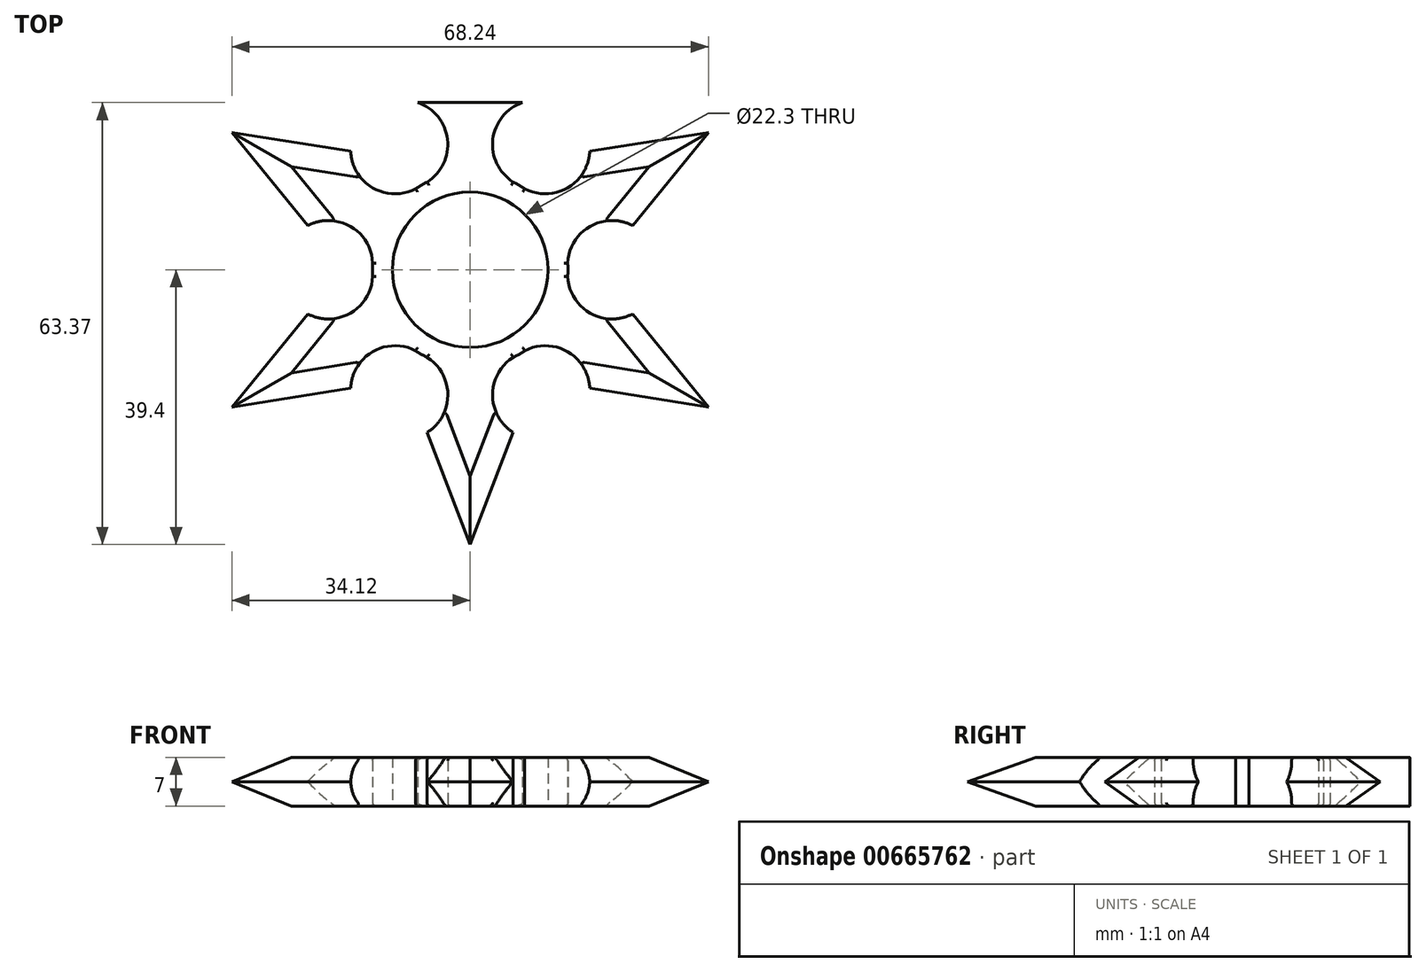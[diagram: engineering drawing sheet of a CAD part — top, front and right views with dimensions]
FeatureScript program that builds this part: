
annotation { "Feature Type Name" : "Feature", "Feature Type Description" : "" }
export const myFeature = defineFeature(function(context is Context, id is Id, definition is map)
    precondition{}
    {
        {
            var Q0;
            Q0=qCreatedBy(makeId("Top.planeOp"),FACE);
            var sketch = newSketch(context, id + "F0", { "sketchPlane" : qUnion([Q0])});
            skCircle(sketch, "E0", {"center": v(0, 0) * mm, "radius": 11.15 * mm});
            skCircle(sketch, "E1", {"center": v(0, 0) * mm, "radius": 14 * mm});
            skLineSegment(sketch, "E2", {"start": v(0, 0) * mm, "end": v(0, 43.6) * mm});
            skLineSegment(sketch, "E3", {"start": v(0, 0) * mm, "end": v(37.76, 21.8) * mm});
            skLineSegment(sketch, "E4.MirrorCS", {"start": v(0, 0) * mm, "end": v(37.76, -21.8) * mm});
            skLineSegment(sketch, "E5.MirrorCS", {"start": v(0, 0) * mm, "end": v(-37.76, -21.8) * mm});
            skLineSegment(sketch, "E6.MirrorCS", {"start": v(0, 0) * mm, "end": v(-37.76, 21.8) * mm});
            skLineSegment(sketch, "E7", {"start": v(0, 0) * mm, "end": v(0, -43.6) * mm});
            skLineSegment(sketch, "E8", {"start": v(37.76, 21.8) * mm, "end": v(24.77, 14.3) * mm});
            skLineSegment(sketch, "E9", {"start": v(37.76, 21.8) * mm, "end": v(20.76, 11.98) * mm});
            skLineSegment(sketch, "E10", {"start": v(20.76, 11.98) * mm, "end": v(24.5, 5.49) * mm});
            skLineSegment(sketch, "E11.MirrorCS", {"start": v(20.76, 11.98) * mm, "end": v(17, 18.48) * mm});
            skLineSegment(sketch, "E12", {"start": v(37.76, 21.8) * mm, "end": v(17, 18.48) * mm});
            skLineSegment(sketch, "E13", {"start": v(24.5, 5.49) * mm, "end": v(37.76, 21.8) * mm});
            skLineSegment(sketch, "E14", {"start": v(0, 0) * mm, "end": v(7, 12.12) * mm});
            skArc(sketch, "E15", {"start": v(7, 12.12) * mm, "mid": v(14.18, 11.88) * mm, "end": v(17, 18.48) * mm});
            skArc(sketch, "E16.MirrorCS", {"start": v(14, 0) * mm, "mid": v(17.38, 6.34) * mm, "end": v(24.5, 5.49) * mm});
            skLineSegment(sketch, "E17.MirrorCS", {"start": v(-37.76, 21.8) * mm, "end": v(-17, 18.48) * mm});
            skLineSegment(sketch, "E18.MirrorCS", {"start": v(-20.76, 11.98) * mm, "end": v(-17, 18.48) * mm});
            skArc(sketch, "E19.MirrorCS", {"start": v(-7, 12.12) * mm, "mid": v(-14.18, 11.88) * mm, "end": v(-17, 18.48) * mm});
            skArc(sketch, "E20.MirrorCS", {"start": v(-14, 0) * mm, "mid": v(-17.38, 6.34) * mm, "end": v(-24.5, 5.49) * mm});
            skLineSegment(sketch, "E21.MirrorCS", {"start": v(-20.76, 11.98) * mm, "end": v(-24.5, 5.49) * mm});
            skLineSegment(sketch, "E22.MirrorCS", {"start": v(-24.5, 5.49) * mm, "end": v(-37.76, 21.8) * mm});
            skArc(sketch, "E23.MirrorCS", {"start": v(7, -12.12) * mm, "mid": v(14.18, -11.88) * mm, "end": v(17, -18.48) * mm});
            skLineSegment(sketch, "E24.MirrorCS", {"start": v(37.76, -21.8) * mm, "end": v(17, -18.48) * mm});
            skLineSegment(sketch, "E25.MirrorCS", {"start": v(20.76, -11.98) * mm, "end": v(17, -18.48) * mm});
            skArc(sketch, "E26.MirrorCS", {"start": v(14, 0) * mm, "mid": v(17.38, -6.34) * mm, "end": v(24.5, -5.49) * mm});
            skLineSegment(sketch, "E27.MirrorCS", {"start": v(20.76, -11.98) * mm, "end": v(24.5, -5.49) * mm});
            skLineSegment(sketch, "E28.MirrorCS", {"start": v(24.5, -5.49) * mm, "end": v(37.76, -21.8) * mm});
            skArc(sketch, "E29.MirrorCS", {"start": v(-14, 0) * mm, "mid": v(-17.38, -6.34) * mm, "end": v(-24.5, -5.49) * mm});
            skLineSegment(sketch, "E30.MirrorCS", {"start": v(-20.76, -11.98) * mm, "end": v(-24.5, -5.49) * mm});
            skLineSegment(sketch, "E31.MirrorCS", {"start": v(-24.5, -5.49) * mm, "end": v(-37.76, -21.8) * mm});
            skLineSegment(sketch, "E32.MirrorCS", {"start": v(-37.76, -21.8) * mm, "end": v(-17, -18.48) * mm});
            skArc(sketch, "E33.MirrorCS", {"start": v(-7, -12.12) * mm, "mid": v(-14.18, -11.88) * mm, "end": v(-17, -18.48) * mm});
            skLineSegment(sketch, "E34.MirrorCS", {"start": v(-20.76, -11.98) * mm, "end": v(-17, -18.48) * mm});
            skLineSegment(sketch, "E35", {"start": v(0, 43.6) * mm, "end": v(0, 23.97) * mm});
            skLineSegment(sketch, "E36", {"start": v(0, 23.97) * mm, "end": v(7.5, 23.97) * mm});
            skLineSegment(sketch, "E37", {"start": v(0, 43.6) * mm, "end": v(7.5, 23.97) * mm});
            skLineSegment(sketch, "E38.MirrorCS", {"start": v(0, 43.6) * mm, "end": v(-7.5, 23.97) * mm});
            skLineSegment(sketch, "E39.MirrorCS", {"start": v(0, 23.97) * mm, "end": v(-7.5, 23.97) * mm});
            skLineSegment(sketch, "E40", {"start": v(0, 0) * mm, "end": v(-7, 12.12) * mm});
            skLineSegment(sketch, "E41.MirrorCS", {"start": v(0, -43.6) * mm, "end": v(-7.5, -23.97) * mm});
            skLineSegment(sketch, "E42.MirrorCS", {"start": v(0, -23.97) * mm, "end": v(-7.5, -23.97) * mm});
            skLineSegment(sketch, "E43.MirrorCS", {"start": v(0, -23.97) * mm, "end": v(7.5, -23.97) * mm});
            skLineSegment(sketch, "E44.MirrorCS", {"start": v(0, -43.6) * mm, "end": v(7.5, -23.97) * mm});
            skArc(sketch, "E45", {"start": v(7, -12.12) * mm, "mid": v(3.2, -18.22) * mm, "end": v(7.5, -23.97) * mm});
            skArc(sketch, "E46.MirrorCS", {"start": v(-7, -12.12) * mm, "mid": v(-3.2, -18.22) * mm, "end": v(-7.5, -23.97) * mm});
            skArc(sketch, "E47.MirrorCS", {"start": v(7, 12.12) * mm, "mid": v(3.2, 18.22) * mm, "end": v(7.5, 23.97) * mm});
            skArc(sketch, "E48.MirrorCS", {"start": v(-7, 12.12) * mm, "mid": v(-3.2, 18.22) * mm, "end": v(-7.5, 23.97) * mm});
            skSolve(sketch);
        }
        {
            var Q0;
            Q0=makeQuery(id+"F0.imprint","IMPRINT",FACE,{"disambiguationData":[TD([[makeQuery(id+"F0.imprint","IMPRINT",EDGE,{"derivedFrom":sQuery(id+"F0.wireOp",EDGE,"E35")}),1.0]])]});
            var Q1;
            Q1=makeQuery(id+"F0.imprint","IMPRINT",FACE,{"disambiguationData":[TD([[makeQuery(id+"F0.imprint","IMPRINT",EDGE,{"derivedFrom":sQuery(id+"F0.wireOp",EDGE,"E35")}),-1.0]])]});
            var Q2;
            {var subQ5=sQuery(id+"F0.wireOp",EDGE,"E39.MirrorCS");Q2=makeQuery(id+"F0.imprint","IMPRINT",FACE,{"disambiguationData":[TD([[makeQuery(id+"F0.imprint","IMPRINT",EDGE,{"derivedFrom":subQ5}),1.0]])]});}
            var Q3;
            {var subQ5=sQuery(id+"F0.wireOp",EDGE,"E36");Q3=makeQuery(id+"F0.imprint","IMPRINT",FACE,{"disambiguationData":[TD([[makeQuery(id+"F0.imprint","IMPRINT",EDGE,{"derivedFrom":subQ5}),-1.0]])]});}
            var Q4;
            {var subQ1=sQuery(id+"F0.wireOp",EDGE,"E0");var subQ7=sQuery(id+"F0.wireOp",EDGE,"E14");var subQ9=makeQuery(id+"F0.imprint","INTERSECT",VERTEX,{"derivedFrom":[subQ1,subQ7]});Q4=makeQuery(id+"F0.imprint","IMPRINT",FACE,{"disambiguationData":[TD([[makeQuery(id+"F0.imprint","IMPRINT",EDGE,{"disambiguationData":[TD([[subQ9,-1.0]])],"derivedFrom":subQ1}),-1.0]])]});}
            var Q5;
            {var subQ4=sQuery(id+"F0.wireOp",EDGE,"E0");var subQ7=sQuery(id+"F0.wireOp",EDGE,"E2");var subQ8=makeQuery(id+"F0.imprint","INTERSECT",VERTEX,{"derivedFrom":[subQ4,subQ7]});Q5=makeQuery(id+"F0.imprint","IMPRINT",FACE,{"disambiguationData":[TD([[makeQuery(id+"F0.imprint","IMPRINT",EDGE,{"disambiguationData":[TD([[subQ8,-1.0]])],"derivedFrom":subQ4}),-1.0]])]});}
            var Q6;
            {var subQ1=sQuery(id+"F0.wireOp",EDGE,"E0");var subQ5=sQuery(id+"F0.wireOp",EDGE,"E40");var subQ6=makeQuery(id+"F0.imprint","INTERSECT",VERTEX,{"derivedFrom":[subQ1,subQ5]});Q6=makeQuery(id+"F0.imprint","IMPRINT",FACE,{"disambiguationData":[TD([[makeQuery(id+"F0.imprint","IMPRINT",EDGE,{"disambiguationData":[TD([[subQ6,-1.0]])],"derivedFrom":subQ1}),-1.0]])]});}
            var Q7;
            {var subQ5=sQuery(id+"F0.wireOp",EDGE,"E18.MirrorCS");Q7=makeQuery(id+"F0.imprint","IMPRINT",FACE,{"disambiguationData":[TD([[makeQuery(id+"F0.imprint","IMPRINT",EDGE,{"derivedFrom":subQ5}),-1.0]])]});}
            var Q8;
            {var subQ5=sQuery(id+"F0.wireOp",EDGE,"E0");var subQ9=sQuery(id+"F0.wireOp",EDGE,"E6.MirrorCS");var subQ11=makeQuery(id+"F0.imprint","INTERSECT",VERTEX,{"derivedFrom":[subQ5,subQ9]});Q8=makeQuery(id+"F0.imprint","IMPRINT",FACE,{"disambiguationData":[TD([[makeQuery(id+"F0.imprint","IMPRINT",EDGE,{"disambiguationData":[TD([[subQ11,-1.0]])],"derivedFrom":subQ5}),-1.0]])]});}
            var Q9;
            {var subQ2=sQuery(id+"F0.wireOp",EDGE,"E30.MirrorCS");Q9=makeQuery(id+"F0.imprint","IMPRINT",FACE,{"disambiguationData":[TD([[makeQuery(id+"F0.imprint","IMPRINT",EDGE,{"derivedFrom":subQ2}),1.0]])]});}
            var Q10;
            {var subQ1=sQuery(id+"F0.wireOp",EDGE,"E14");var subQ4=sQuery(id+"F0.wireOp",EDGE,"E0");var subQ5=makeQuery(id+"F0.imprint","INTERSECT",VERTEX,{"derivedFrom":[subQ4,subQ1]});Q10=makeQuery(id+"F0.imprint","IMPRINT",FACE,{"disambiguationData":[TD([[makeQuery(id+"F0.imprint","IMPRINT",EDGE,{"disambiguationData":[TD([[subQ5,1.0]])],"derivedFrom":subQ4}),-1.0]])]});}
            var Q11;
            {var subQ5=sQuery(id+"F0.wireOp",EDGE,"E43.MirrorCS");Q11=makeQuery(id+"F0.imprint","IMPRINT",FACE,{"disambiguationData":[TD([[makeQuery(id+"F0.imprint","IMPRINT",EDGE,{"derivedFrom":subQ5}),1.0]])]});}
            var Q12;
            {var subQ5=sQuery(id+"F0.wireOp",EDGE,"E7");var subQ6=sQuery(id+"F0.wireOp",EDGE,"E0");var subQ7=makeQuery(id+"F0.imprint","INTERSECT",VERTEX,{"derivedFrom":[subQ6,subQ5]});Q12=makeQuery(id+"F0.imprint","IMPRINT",FACE,{"disambiguationData":[TD([[makeQuery(id+"F0.imprint","IMPRINT",EDGE,{"disambiguationData":[TD([[subQ7,-1.0]])],"derivedFrom":subQ6}),-1.0]])]});}
            var Q13;
            {var subQ5=sQuery(id+"F0.wireOp",EDGE,"E21.MirrorCS");Q13=makeQuery(id+"F0.imprint","IMPRINT",FACE,{"disambiguationData":[TD([[makeQuery(id+"F0.imprint","IMPRINT",EDGE,{"derivedFrom":subQ5}),1.0]])]});}
            var Q14;
            {var subQ5=sQuery(id+"F0.wireOp",EDGE,"E34.MirrorCS");Q14=makeQuery(id+"F0.imprint","IMPRINT",FACE,{"disambiguationData":[TD([[makeQuery(id+"F0.imprint","IMPRINT",EDGE,{"derivedFrom":subQ5}),1.0]])]});}
            var Q15;
            {var subQ5=sQuery(id+"F0.wireOp",EDGE,"E25.MirrorCS");Q15=makeQuery(id+"F0.imprint","IMPRINT",FACE,{"disambiguationData":[TD([[makeQuery(id+"F0.imprint","IMPRINT",EDGE,{"derivedFrom":subQ5}),-1.0]])]});}
            var Q16;
            {var subQ2=sQuery(id+"F0.wireOp",EDGE,"E27.MirrorCS");Q16=makeQuery(id+"F0.imprint","IMPRINT",FACE,{"disambiguationData":[TD([[makeQuery(id+"F0.imprint","IMPRINT",EDGE,{"derivedFrom":subQ2}),-1.0]])]});}
            var Q17;
            {var subQ0=sQuery(id+"F0.wireOp",EDGE,"E24.MirrorCS");Q17=makeQuery(id+"F0.imprint","IMPRINT",FACE,{"disambiguationData":[TD([[makeQuery(id+"F0.imprint","IMPRINT",EDGE,{"derivedFrom":subQ0}),-1.0]])]});}
            var Q18;
            {var subQ5=sQuery(id+"F0.wireOp",EDGE,"E42.MirrorCS");Q18=makeQuery(id+"F0.imprint","IMPRINT",FACE,{"disambiguationData":[TD([[makeQuery(id+"F0.imprint","IMPRINT",EDGE,{"derivedFrom":subQ5}),-1.0]])]});}
            var Q19;
            {var subQ5=sQuery(id+"F0.wireOp",EDGE,"E10");Q19=makeQuery(id+"F0.imprint","IMPRINT",FACE,{"disambiguationData":[TD([[makeQuery(id+"F0.imprint","IMPRINT",EDGE,{"derivedFrom":subQ5}),-1.0]])]});}
            var Q20;
            {var subQ2=sQuery(id+"F0.wireOp",EDGE,"E21.MirrorCS");Q20=makeQuery(id+"F0.imprint","IMPRINT",FACE,{"disambiguationData":[TD([[makeQuery(id+"F0.imprint","IMPRINT",EDGE,{"derivedFrom":subQ2}),-1.0]])]});}
            var Q21;
            {var subQ0=sQuery(id+"F0.wireOp",EDGE,"E5.MirrorCS");var subQ1=sQuery(id+"F0.wireOp",EDGE,"E0");var subQ2=makeQuery(id+"F0.imprint","INTERSECT",VERTEX,{"derivedFrom":[subQ1,subQ0]});Q21=makeQuery(id+"F0.imprint","IMPRINT",FACE,{"disambiguationData":[TD([[makeQuery(id+"F0.imprint","IMPRINT",EDGE,{"disambiguationData":[TD([[subQ2,-1.0]])],"derivedFrom":subQ1}),-1.0]])]});}
            var Q22;
            {var subQ5=sQuery(id+"F0.wireOp",EDGE,"E11.MirrorCS");Q22=makeQuery(id+"F0.imprint","IMPRINT",FACE,{"disambiguationData":[TD([[makeQuery(id+"F0.imprint","IMPRINT",EDGE,{"derivedFrom":subQ5}),1.0]])]});}
            var Q23;
            {var subQ5=sQuery(id+"F0.wireOp",EDGE,"E27.MirrorCS");Q23=makeQuery(id+"F0.imprint","IMPRINT",FACE,{"disambiguationData":[TD([[makeQuery(id+"F0.imprint","IMPRINT",EDGE,{"derivedFrom":subQ5}),1.0]])]});}
            var Q24;
            {var subQ3=sQuery(id+"F0.wireOp",EDGE,"E11.MirrorCS");Q24=makeQuery(id+"F0.imprint","IMPRINT",FACE,{"disambiguationData":[TD([[makeQuery(id+"F0.imprint","IMPRINT",EDGE,{"derivedFrom":subQ3}),-1.0]])]});}
            var Q25;
            {var subQ0=sQuery(id+"F0.wireOp",EDGE,"E17.MirrorCS");Q25=makeQuery(id+"F0.imprint","IMPRINT",FACE,{"disambiguationData":[TD([[makeQuery(id+"F0.imprint","IMPRINT",EDGE,{"derivedFrom":subQ0}),-1.0]])]});}
            var Q26;
            {var subQ0=sQuery(id+"F0.wireOp",EDGE,"E32.MirrorCS");Q26=makeQuery(id+"F0.imprint","IMPRINT",FACE,{"disambiguationData":[TD([[makeQuery(id+"F0.imprint","IMPRINT",EDGE,{"derivedFrom":subQ0}),1.0]])]});}
            var Q27;
            {var subQ5=sQuery(id+"F0.wireOp",EDGE,"E30.MirrorCS");Q27=makeQuery(id+"F0.imprint","IMPRINT",FACE,{"disambiguationData":[TD([[makeQuery(id+"F0.imprint","IMPRINT",EDGE,{"derivedFrom":subQ5}),-1.0]])]});}
            var Q28;
            {var subQ3=sQuery(id+"F0.wireOp",EDGE,"E10");Q28=makeQuery(id+"F0.imprint","IMPRINT",FACE,{"disambiguationData":[TD([[makeQuery(id+"F0.imprint","IMPRINT",EDGE,{"derivedFrom":subQ3}),1.0]])]});}
            var Q29;
            {var subQ0=sQuery(id+"F0.wireOp",EDGE,"E41.MirrorCS");Q29=makeQuery(id+"F0.imprint","IMPRINT",FACE,{"disambiguationData":[TD([[makeQuery(id+"F0.imprint","IMPRINT",EDGE,{"derivedFrom":subQ0}),-1.0]])]});}
            var Q30;
            {var subQ1=sQuery(id+"F0.wireOp",EDGE,"E0");var subQ9=sQuery(id+"F0.wireOp",EDGE,"E3");var subQ12=makeQuery(id+"F0.imprint","INTERSECT",VERTEX,{"derivedFrom":[subQ1,subQ9]});Q30=makeQuery(id+"F0.imprint","IMPRINT",FACE,{"disambiguationData":[TD([[makeQuery(id+"F0.imprint","IMPRINT",EDGE,{"disambiguationData":[TD([[subQ12,1.0]])],"derivedFrom":subQ1}),-1.0]])]});}
            var Q31;
            {var subQ2=sQuery(id+"F0.wireOp",EDGE,"E43.MirrorCS");Q31=makeQuery(id+"F0.imprint","IMPRINT",FACE,{"disambiguationData":[TD([[makeQuery(id+"F0.imprint","IMPRINT",EDGE,{"derivedFrom":subQ2}),-1.0]])]});}
            var Q32;
            {var subQ0=sQuery(id+"F0.wireOp",EDGE,"E45");var subQ1=sQuery(id+"F0.wireOp",EDGE,"E1");var subQ3=makeQuery(id+"F0.imprint","INTERSECT",VERTEX,{"derivedFrom":[subQ1,subQ0]});Q32=makeQuery(id+"F0.imprint","IMPRINT",FACE,{"disambiguationData":[TD([[makeQuery(id+"F0.imprint","IMPRINT",EDGE,{"disambiguationData":[TD([[subQ3,-1.0]])],"derivedFrom":subQ1}),1.0]])]});}
            var Q33;
            {var subQ0=sQuery(id+"F0.wireOp",EDGE,"E26.MirrorCS");var subQ1=sQuery(id+"F0.wireOp",EDGE,"E1");var subQ3=makeQuery(id+"F0.imprint","INTERSECT",VERTEX,{"derivedFrom":[subQ1,subQ0]});Q33=makeQuery(id+"F0.imprint","IMPRINT",FACE,{"disambiguationData":[TD([[makeQuery(id+"F0.imprint","IMPRINT",EDGE,{"disambiguationData":[TD([[subQ3,-1.0]])],"derivedFrom":subQ1}),1.0]])]});}
            var Q34;
            {var subQ0=sQuery(id+"F0.wireOp",EDGE,"E23.MirrorCS");var subQ1=sQuery(id+"F0.wireOp",EDGE,"E1");var subQ3=makeQuery(id+"F0.imprint","INTERSECT",VERTEX,{"derivedFrom":[subQ1,subQ0]});Q34=makeQuery(id+"F0.imprint","IMPRINT",FACE,{"disambiguationData":[TD([[makeQuery(id+"F0.imprint","IMPRINT",EDGE,{"disambiguationData":[TD([[subQ3,1.0]])],"derivedFrom":subQ1}),1.0]])]});}
            var Q35;
            {var subQ0=sQuery(id+"F0.wireOp",EDGE,"E33.MirrorCS");var subQ1=sQuery(id+"F0.wireOp",EDGE,"E1");var subQ3=makeQuery(id+"F0.imprint","INTERSECT",VERTEX,{"derivedFrom":[subQ1,subQ0]});Q35=makeQuery(id+"F0.imprint","IMPRINT",FACE,{"disambiguationData":[TD([[makeQuery(id+"F0.imprint","IMPRINT",EDGE,{"disambiguationData":[TD([[subQ3,-1.0]])],"derivedFrom":subQ1}),1.0]])]});}
            var Q36;
            {var subQ0=sQuery(id+"F0.wireOp",EDGE,"E46.MirrorCS");var subQ1=sQuery(id+"F0.wireOp",EDGE,"E1");var subQ3=makeQuery(id+"F0.imprint","INTERSECT",VERTEX,{"derivedFrom":[subQ1,subQ0]});Q36=makeQuery(id+"F0.imprint","IMPRINT",FACE,{"disambiguationData":[TD([[makeQuery(id+"F0.imprint","IMPRINT",EDGE,{"disambiguationData":[TD([[subQ3,1.0]])],"derivedFrom":subQ1}),1.0]])]});}
            var Q37;
            {var subQ0=sQuery(id+"F0.wireOp",EDGE,"E29.MirrorCS");var subQ1=sQuery(id+"F0.wireOp",EDGE,"E1");var subQ3=makeQuery(id+"F0.imprint","INTERSECT",VERTEX,{"derivedFrom":[subQ1,subQ0]});Q37=makeQuery(id+"F0.imprint","IMPRINT",FACE,{"disambiguationData":[TD([[makeQuery(id+"F0.imprint","IMPRINT",EDGE,{"disambiguationData":[TD([[subQ3,1.0]])],"derivedFrom":subQ1}),1.0]])]});}
            var Q38;
            {var subQ0=sQuery(id+"F0.wireOp",EDGE,"E20.MirrorCS");var subQ1=sQuery(id+"F0.wireOp",EDGE,"E1");var subQ3=makeQuery(id+"F0.imprint","INTERSECT",VERTEX,{"derivedFrom":[subQ1,subQ0]});Q38=makeQuery(id+"F0.imprint","IMPRINT",FACE,{"disambiguationData":[TD([[makeQuery(id+"F0.imprint","IMPRINT",EDGE,{"disambiguationData":[TD([[subQ3,-1.0]])],"derivedFrom":subQ1}),1.0]])]});}
            var Q39;
            {var subQ0=sQuery(id+"F0.wireOp",EDGE,"E16.MirrorCS");var subQ1=sQuery(id+"F0.wireOp",EDGE,"E1");var subQ3=makeQuery(id+"F0.imprint","INTERSECT",VERTEX,{"derivedFrom":[subQ1,subQ0]});Q39=makeQuery(id+"F0.imprint","IMPRINT",FACE,{"disambiguationData":[TD([[makeQuery(id+"F0.imprint","IMPRINT",EDGE,{"disambiguationData":[TD([[subQ3,1.0]])],"derivedFrom":subQ1}),1.0]])]});}
            var Q40;
            {var subQ0=sQuery(id+"F0.wireOp",EDGE,"E48.MirrorCS");var subQ1=sQuery(id+"F0.wireOp",EDGE,"E1");var subQ3=makeQuery(id+"F0.imprint","INTERSECT",VERTEX,{"derivedFrom":[subQ1,subQ0]});Q40=makeQuery(id+"F0.imprint","IMPRINT",FACE,{"disambiguationData":[TD([[makeQuery(id+"F0.imprint","IMPRINT",EDGE,{"disambiguationData":[TD([[subQ3,-1.0]])],"derivedFrom":subQ1}),1.0]])]});}
            var Q41;
            {var subQ0=sQuery(id+"F0.wireOp",EDGE,"E19.MirrorCS");var subQ1=sQuery(id+"F0.wireOp",EDGE,"E1");var subQ3=makeQuery(id+"F0.imprint","INTERSECT",VERTEX,{"derivedFrom":[subQ1,subQ0]});Q41=makeQuery(id+"F0.imprint","IMPRINT",FACE,{"disambiguationData":[TD([[makeQuery(id+"F0.imprint","IMPRINT",EDGE,{"disambiguationData":[TD([[subQ3,1.0]])],"derivedFrom":subQ1}),1.0]])]});}
            var Q42;
            {var subQ0=sQuery(id+"F0.wireOp",EDGE,"E47.MirrorCS");var subQ1=sQuery(id+"F0.wireOp",EDGE,"E1");var subQ3=makeQuery(id+"F0.imprint","INTERSECT",VERTEX,{"derivedFrom":[subQ1,subQ0]});Q42=makeQuery(id+"F0.imprint","IMPRINT",FACE,{"disambiguationData":[TD([[makeQuery(id+"F0.imprint","IMPRINT",EDGE,{"disambiguationData":[TD([[subQ3,1.0]])],"derivedFrom":subQ1}),1.0]])]});}
            var Q43;
            {var subQ0=sQuery(id+"F0.wireOp",EDGE,"E15");var subQ1=sQuery(id+"F0.wireOp",EDGE,"E1");var subQ3=makeQuery(id+"F0.imprint","INTERSECT",VERTEX,{"derivedFrom":[subQ1,subQ0]});Q43=makeQuery(id+"F0.imprint","IMPRINT",FACE,{"disambiguationData":[TD([[makeQuery(id+"F0.imprint","IMPRINT",EDGE,{"disambiguationData":[TD([[subQ3,-1.0]])],"derivedFrom":subQ1}),1.0]])]});}
            var Q44;
            Q44=makeQuery(id+"F0.imprint","IMPRINT",FACE,{"disambiguationData":[TD([[makeQuery(id+"F0.imprint","IMPRINT",EDGE,{"derivedFrom":sQuery(id+"F0.wireOp",EDGE,"p3hnCSgG-ZrtL-qWsR-BndH-5srnAVTTJyzc")}),1.0]])]});
            extrude(context, id + "F1", {"entities" : qUnion([Q0, Q1, Q2, Q3, Q4, Q5, Q6, Q7, Q8, Q9, Q10, Q11, Q12, Q13, Q14, Q15, Q16, Q17, Q18, Q19, Q20, Q21, Q22, Q23, Q24, Q25, Q26, Q27, Q28, Q29, Q30, Q31, Q32, Q33, Q34, Q35, Q36, Q37, Q38, Q39, Q40, Q41, Q42, Q43, Q44]), "depth" : 7 * mm, "offsetDistance" : 25 * mm});
        }
        {
            var Q0;
            Q0=makeQuery(id+"F1.opExtrude","CAP_EDGE",EDGE,{"disambiguationData":[OSD([sQuery(id+"F0.wireOp",EDGE,"E24.MirrorCS")])],"isStart":false});
            var Q1;
            Q1=makeQuery(id+"F1.opExtrude","CAP_EDGE",EDGE,{"disambiguationData":[OSD([sQuery(id+"F0.wireOp",EDGE,"E28.MirrorCS")])],"isStart":false});
            var Q2;
            Q2=makeQuery(id+"F1.opExtrude","CAP_EDGE",EDGE,{"disambiguationData":[OSD([sQuery(id+"F0.wireOp",EDGE,"E44.MirrorCS")])],"isStart":false});
            var Q3;
            Q3=makeQuery(id+"F1.opExtrude","CAP_EDGE",EDGE,{"disambiguationData":[OSD([sQuery(id+"F0.wireOp",EDGE,"E32.MirrorCS")])],"isStart":false});
            var Q4;
            Q4=makeQuery(id+"F1.opExtrude","CAP_EDGE",EDGE,{"disambiguationData":[OSD([sQuery(id+"F0.wireOp",EDGE,"E22.MirrorCS")])],"isStart":false});
            var Q5;
            Q5=makeQuery(id+"F1.opExtrude","CAP_EDGE",EDGE,{"disambiguationData":[OSD([sQuery(id+"F0.wireOp",EDGE,"E38.MirrorCS")])],"isStart":false});
            var Q6;
            Q6=makeQuery(id+"F1.opExtrude","CAP_EDGE",EDGE,{"disambiguationData":[OSD([sQuery(id+"F0.wireOp",EDGE,"E12")])],"isStart":false});
            chamfer(context, id + "F2", {"entities" : qUnion([Q0, Q1, Q2, Q3, Q4, Q5, Q6]), "width" : 5 * mm, "tangentPropagation" : true});
        }
        {
            var Q0;
            Q0=makeQuery(id+"F1.opExtrude","CAP_EDGE",EDGE,{"disambiguationData":[OSD([sQuery(id+"F0.wireOp",EDGE,"E37")])],"isStart":false});
            var Q1;
            Q1=makeQuery(id+"F1.opExtrude","CAP_EDGE",EDGE,{"disambiguationData":[OSD([sQuery(id+"F0.wireOp",EDGE,"E17.MirrorCS")])],"isStart":false});
            var Q2;
            Q2=makeQuery(id+"F1.opExtrude","CAP_EDGE",EDGE,{"disambiguationData":[OSD([sQuery(id+"F0.wireOp",EDGE,"E31.MirrorCS")])],"isStart":false});
            var Q3;
            Q3=makeQuery(id+"F1.opExtrude","CAP_EDGE",EDGE,{"disambiguationData":[OSD([sQuery(id+"F0.wireOp",EDGE,"E41.MirrorCS")])],"isStart":false});
            var Q4;
            Q4=makeQuery(id+"F1.opExtrude","CAP_EDGE",EDGE,{"disambiguationData":[OSD([sQuery(id+"F0.wireOp",EDGE,"E13")])],"isStart":false});
            chamfer(context, id + "F3", {"entities" : qUnion([Q0, Q1, Q2, Q3, Q4]), "width" : 5 * mm, "tangentPropagation" : true});
        }
        {
            var Q0;
            Q0=makeQuery(id+"F1.opExtrude","CAP_EDGE",EDGE,{"disambiguationData":[OSD([sQuery(id+"F0.wireOp",EDGE,"E41.MirrorCS")])],"isStart":true});
            var Q1;
            Q1=makeQuery(id+"F1.opExtrude","CAP_EDGE",EDGE,{"disambiguationData":[OSD([sQuery(id+"F0.wireOp",EDGE,"E24.MirrorCS")])],"isStart":true});
            var Q2;
            Q2=makeQuery(id+"F1.opExtrude","CAP_EDGE",EDGE,{"disambiguationData":[OSD([sQuery(id+"F0.wireOp",EDGE,"E13")])],"isStart":true});
            var Q3;
            Q3=makeQuery(id+"F1.opExtrude","CAP_EDGE",EDGE,{"disambiguationData":[OSD([sQuery(id+"F0.wireOp",EDGE,"E37")])],"isStart":true});
            var Q4;
            Q4=makeQuery(id+"F1.opExtrude","CAP_EDGE",EDGE,{"disambiguationData":[OSD([sQuery(id+"F0.wireOp",EDGE,"E17.MirrorCS")])],"isStart":true});
            var Q5;
            Q5=makeQuery(id+"F1.opExtrude","CAP_EDGE",EDGE,{"disambiguationData":[OSD([sQuery(id+"F0.wireOp",EDGE,"E31.MirrorCS")])],"isStart":true});
            chamfer(context, id + "F4", {"entities" : qUnion([Q0, Q1, Q2, Q3, Q4, Q5]), "width" : 5 * mm, "tangentPropagation" : true});
        }
        {
            var Q0;
            Q0=makeQuery(id+"F1.opExtrude","CAP_EDGE",EDGE,{"disambiguationData":[OSD([sQuery(id+"F0.wireOp",EDGE,"E22.MirrorCS")])],"isStart":true});
            var Q1;
            Q1=makeQuery(id+"F1.opExtrude","CAP_EDGE",EDGE,{"disambiguationData":[OSD([sQuery(id+"F0.wireOp",EDGE,"E32.MirrorCS")])],"isStart":true});
            var Q2;
            Q2=makeQuery(id+"F1.opExtrude","CAP_EDGE",EDGE,{"disambiguationData":[OSD([sQuery(id+"F0.wireOp",EDGE,"E44.MirrorCS")])],"isStart":true});
            var Q3;
            Q3=makeQuery(id+"F1.opExtrude","CAP_EDGE",EDGE,{"disambiguationData":[OSD([sQuery(id+"F0.wireOp",EDGE,"E28.MirrorCS")])],"isStart":true});
            var Q4;
            Q4=makeQuery(id+"F1.opExtrude","CAP_EDGE",EDGE,{"disambiguationData":[OSD([sQuery(id+"F0.wireOp",EDGE,"E12")])],"isStart":true});
            var Q5;
            Q5=makeQuery(id+"F1.opExtrude","CAP_EDGE",EDGE,{"disambiguationData":[OSD([sQuery(id+"F0.wireOp",EDGE,"E38.MirrorCS")])],"isStart":true});
            chamfer(context, id + "F5", {"entities" : qUnion([Q0, Q1, Q2, Q3, Q4, Q5]), "width" : 5 * mm, "tangentPropagation" : true});
        }
        {
            var Q0;
            Q0=makeQuery(id+"F1.opExtrude","CAP_EDGE",EDGE,{"disambiguationData":[OSD([sQuery(id+"F0.wireOp",EDGE,"E29.MirrorCS")])],"isStart":false});
            var Q1;
            {var subQ0=sQuery(id+"F0.wireOp",EDGE,"E29.MirrorCS");var subQ1=sQuery(id+"F0.wireOp",EDGE,"E20.MirrorCS");var subQ2=sQuery(id+"F0.wireOp",EDGE,"E1");Q1=makeQuery(id+"F1.opExtrude","CAP_EDGE",EDGE,{"disambiguationData":[OSD([subQ2]),TDD([makeQuery(id+"F0.imprint","IMPRINT",EDGE,{"disambiguationData":[TD([[makeQuery(id+"F0.imprint","INTERSECT",VERTEX,{"derivedFrom":[subQ2,subQ1]}),-1.0]])],"derivedFrom":subQ2}),makeQuery(id+"F0.imprint","IMPRINT",EDGE,{"disambiguationData":[TD([[makeQuery(id+"F0.imprint","INTERSECT",VERTEX,{"derivedFrom":[subQ2,subQ0]}),1.0]])],"derivedFrom":subQ2})])],"isStart":false});}
            var Q2;
            Q2=makeQuery(id+"F1.opExtrude","CAP_EDGE",EDGE,{"disambiguationData":[OSD([sQuery(id+"F0.wireOp",EDGE,"E20.MirrorCS")])],"isStart":false});
            var Q3;
            Q3=makeQuery(id+"F1.opExtrude","CAP_EDGE",EDGE,{"disambiguationData":[OSD([sQuery(id+"F0.wireOp",EDGE,"E19.MirrorCS")])],"isStart":false});
            var Q4;
            {var subQ0=sQuery(id+"F0.wireOp",EDGE,"E48.MirrorCS");var subQ1=sQuery(id+"F0.wireOp",EDGE,"E19.MirrorCS");var subQ2=sQuery(id+"F0.wireOp",EDGE,"E1");Q4=makeQuery(id+"F1.opExtrude","CAP_EDGE",EDGE,{"disambiguationData":[OSD([subQ2]),TDD([makeQuery(id+"F0.imprint","IMPRINT",EDGE,{"disambiguationData":[TD([[makeQuery(id+"F0.imprint","INTERSECT",VERTEX,{"derivedFrom":[subQ2,subQ0]}),-1.0]])],"derivedFrom":subQ2}),makeQuery(id+"F0.imprint","IMPRINT",EDGE,{"disambiguationData":[TD([[makeQuery(id+"F0.imprint","INTERSECT",VERTEX,{"derivedFrom":[subQ2,subQ1]}),1.0]])],"derivedFrom":subQ2})])],"isStart":false});}
            var Q5;
            Q5=makeQuery(id+"F1.opExtrude","CAP_EDGE",EDGE,{"disambiguationData":[OSD([sQuery(id+"F0.wireOp",EDGE,"E48.MirrorCS")])],"isStart":false});
            var Q6;
            Q6=makeQuery(id+"F1.opExtrude","CAP_EDGE",EDGE,{"disambiguationData":[OSD([sQuery(id+"F0.wireOp",EDGE,"E47.MirrorCS")])],"isStart":false});
            var Q7;
            {var subQ0=sQuery(id+"F0.wireOp",EDGE,"E47.MirrorCS");var subQ1=sQuery(id+"F0.wireOp",EDGE,"E15");var subQ2=sQuery(id+"F0.wireOp",EDGE,"E1");Q7=makeQuery(id+"F1.opExtrude","CAP_EDGE",EDGE,{"disambiguationData":[OSD([subQ2]),TDD([makeQuery(id+"F0.imprint","IMPRINT",EDGE,{"disambiguationData":[TD([[makeQuery(id+"F0.imprint","INTERSECT",VERTEX,{"derivedFrom":[subQ2,subQ1]}),-1.0]])],"derivedFrom":subQ2}),makeQuery(id+"F0.imprint","IMPRINT",EDGE,{"disambiguationData":[TD([[makeQuery(id+"F0.imprint","INTERSECT",VERTEX,{"derivedFrom":[subQ2,subQ0]}),1.0]])],"derivedFrom":subQ2})])],"isStart":false});}
            var Q8;
            Q8=makeQuery(id+"F1.opExtrude","CAP_EDGE",EDGE,{"disambiguationData":[OSD([sQuery(id+"F0.wireOp",EDGE,"E15")])],"isStart":false});
            var Q9;
            Q9=makeQuery(id+"F1.opExtrude","CAP_EDGE",EDGE,{"disambiguationData":[OSD([sQuery(id+"F0.wireOp",EDGE,"E16.MirrorCS")])],"isStart":false});
            var Q10;
            {var subQ0=sQuery(id+"F0.wireOp",EDGE,"E26.MirrorCS");var subQ1=sQuery(id+"F0.wireOp",EDGE,"E16.MirrorCS");var subQ2=sQuery(id+"F0.wireOp",EDGE,"E1");Q10=makeQuery(id+"F1.opExtrude","CAP_EDGE",EDGE,{"disambiguationData":[OSD([subQ2]),TDD([makeQuery(id+"F0.imprint","IMPRINT",EDGE,{"disambiguationData":[TD([[makeQuery(id+"F0.imprint","INTERSECT",VERTEX,{"derivedFrom":[subQ2,subQ1]}),1.0]])],"derivedFrom":subQ2}),makeQuery(id+"F0.imprint","IMPRINT",EDGE,{"disambiguationData":[TD([[makeQuery(id+"F0.imprint","INTERSECT",VERTEX,{"derivedFrom":[subQ2,subQ0]}),-1.0]])],"derivedFrom":subQ2})])],"isStart":false});}
            var Q11;
            Q11=makeQuery(id+"F1.opExtrude","CAP_EDGE",EDGE,{"disambiguationData":[OSD([sQuery(id+"F0.wireOp",EDGE,"E26.MirrorCS")])],"isStart":false});
            var Q12;
            Q12=makeQuery(id+"F1.opExtrude","CAP_EDGE",EDGE,{"disambiguationData":[OSD([sQuery(id+"F0.wireOp",EDGE,"E23.MirrorCS")])],"isStart":false});
            var Q13;
            {var subQ0=sQuery(id+"F0.wireOp",EDGE,"E45");var subQ1=sQuery(id+"F0.wireOp",EDGE,"E23.MirrorCS");var subQ2=sQuery(id+"F0.wireOp",EDGE,"E1");Q13=makeQuery(id+"F1.opExtrude","CAP_EDGE",EDGE,{"disambiguationData":[OSD([subQ2]),TDD([makeQuery(id+"F0.imprint","IMPRINT",EDGE,{"disambiguationData":[TD([[makeQuery(id+"F0.imprint","INTERSECT",VERTEX,{"derivedFrom":[subQ2,subQ0]}),-1.0]])],"derivedFrom":subQ2}),makeQuery(id+"F0.imprint","IMPRINT",EDGE,{"disambiguationData":[TD([[makeQuery(id+"F0.imprint","INTERSECT",VERTEX,{"derivedFrom":[subQ2,subQ1]}),1.0]])],"derivedFrom":subQ2})])],"isStart":false});}
            var Q14;
            Q14=makeQuery(id+"F1.opExtrude","CAP_EDGE",EDGE,{"disambiguationData":[OSD([sQuery(id+"F0.wireOp",EDGE,"E45")])],"isStart":false});
            var Q15;
            Q15=makeQuery(id+"F1.opExtrude","CAP_EDGE",EDGE,{"disambiguationData":[OSD([sQuery(id+"F0.wireOp",EDGE,"E46.MirrorCS")])],"isStart":false});
            var Q16;
            {var subQ0=sQuery(id+"F0.wireOp",EDGE,"E46.MirrorCS");var subQ1=sQuery(id+"F0.wireOp",EDGE,"E33.MirrorCS");var subQ2=sQuery(id+"F0.wireOp",EDGE,"E1");Q16=makeQuery(id+"F1.opExtrude","CAP_EDGE",EDGE,{"disambiguationData":[OSD([subQ2]),TDD([makeQuery(id+"F0.imprint","IMPRINT",EDGE,{"disambiguationData":[TD([[makeQuery(id+"F0.imprint","INTERSECT",VERTEX,{"derivedFrom":[subQ2,subQ1]}),-1.0]])],"derivedFrom":subQ2}),makeQuery(id+"F0.imprint","IMPRINT",EDGE,{"disambiguationData":[TD([[makeQuery(id+"F0.imprint","INTERSECT",VERTEX,{"derivedFrom":[subQ2,subQ0]}),1.0]])],"derivedFrom":subQ2})])],"isStart":false});}
            var Q17;
            Q17=makeQuery(id+"F1.opExtrude","CAP_EDGE",EDGE,{"disambiguationData":[OSD([sQuery(id+"F0.wireOp",EDGE,"E33.MirrorCS")])],"isStart":false});
            fillet(context, id + "F6", {"entities" : qUnion([Q0, Q1, Q2, Q3, Q4, Q5, Q6, Q7, Q8, Q9, Q10, Q11, Q12, Q13, Q14, Q15, Q16, Q17]), "radius" : .5 * mm, "tangentPropagation" : true, "allowEdgeOverflow" : false});
        }
        {
            var Q0;
            Q0=makeQuery(id+"F1.opExtrude","CAP_EDGE",EDGE,{"disambiguationData":[OSD([sQuery(id+"F0.wireOp",EDGE,"E48.MirrorCS")])],"isStart":true});
            var Q1;
            {var subQ0=sQuery(id+"F0.wireOp",EDGE,"E48.MirrorCS");var subQ1=sQuery(id+"F0.wireOp",EDGE,"E19.MirrorCS");var subQ2=sQuery(id+"F0.wireOp",EDGE,"E1");Q1=makeQuery(id+"F1.opExtrude","CAP_EDGE",EDGE,{"disambiguationData":[OSD([subQ2]),TDD([makeQuery(id+"F0.imprint","IMPRINT",EDGE,{"disambiguationData":[TD([[makeQuery(id+"F0.imprint","INTERSECT",VERTEX,{"derivedFrom":[subQ2,subQ0]}),-1.0]])],"derivedFrom":subQ2}),makeQuery(id+"F0.imprint","IMPRINT",EDGE,{"disambiguationData":[TD([[makeQuery(id+"F0.imprint","INTERSECT",VERTEX,{"derivedFrom":[subQ2,subQ1]}),1.0]])],"derivedFrom":subQ2})])],"isStart":true});}
            var Q2;
            Q2=makeQuery(id+"F1.opExtrude","CAP_EDGE",EDGE,{"disambiguationData":[OSD([sQuery(id+"F0.wireOp",EDGE,"E19.MirrorCS")])],"isStart":true});
            var Q3;
            Q3=makeQuery(id+"F1.opExtrude","CAP_EDGE",EDGE,{"disambiguationData":[OSD([sQuery(id+"F0.wireOp",EDGE,"E20.MirrorCS")])],"isStart":true});
            var Q4;
            {var subQ0=sQuery(id+"F0.wireOp",EDGE,"E29.MirrorCS");var subQ1=sQuery(id+"F0.wireOp",EDGE,"E20.MirrorCS");var subQ2=sQuery(id+"F0.wireOp",EDGE,"E1");Q4=makeQuery(id+"F1.opExtrude","CAP_EDGE",EDGE,{"disambiguationData":[OSD([subQ2]),TDD([makeQuery(id+"F0.imprint","IMPRINT",EDGE,{"disambiguationData":[TD([[makeQuery(id+"F0.imprint","INTERSECT",VERTEX,{"derivedFrom":[subQ2,subQ1]}),-1.0]])],"derivedFrom":subQ2}),makeQuery(id+"F0.imprint","IMPRINT",EDGE,{"disambiguationData":[TD([[makeQuery(id+"F0.imprint","INTERSECT",VERTEX,{"derivedFrom":[subQ2,subQ0]}),1.0]])],"derivedFrom":subQ2})])],"isStart":true});}
            var Q5;
            Q5=makeQuery(id+"F1.opExtrude","CAP_EDGE",EDGE,{"disambiguationData":[OSD([sQuery(id+"F0.wireOp",EDGE,"E29.MirrorCS")])],"isStart":true});
            var Q6;
            Q6=makeQuery(id+"F1.opExtrude","CAP_EDGE",EDGE,{"disambiguationData":[OSD([sQuery(id+"F0.wireOp",EDGE,"E33.MirrorCS")])],"isStart":true});
            var Q7;
            {var subQ0=sQuery(id+"F0.wireOp",EDGE,"E46.MirrorCS");var subQ1=sQuery(id+"F0.wireOp",EDGE,"E33.MirrorCS");var subQ2=sQuery(id+"F0.wireOp",EDGE,"E1");Q7=makeQuery(id+"F1.opExtrude","CAP_EDGE",EDGE,{"disambiguationData":[OSD([subQ2]),TDD([makeQuery(id+"F0.imprint","IMPRINT",EDGE,{"disambiguationData":[TD([[makeQuery(id+"F0.imprint","INTERSECT",VERTEX,{"derivedFrom":[subQ2,subQ1]}),-1.0]])],"derivedFrom":subQ2}),makeQuery(id+"F0.imprint","IMPRINT",EDGE,{"disambiguationData":[TD([[makeQuery(id+"F0.imprint","INTERSECT",VERTEX,{"derivedFrom":[subQ2,subQ0]}),1.0]])],"derivedFrom":subQ2})])],"isStart":true});}
            var Q8;
            Q8=makeQuery(id+"F1.opExtrude","CAP_EDGE",EDGE,{"disambiguationData":[OSD([sQuery(id+"F0.wireOp",EDGE,"E46.MirrorCS")])],"isStart":true});
            var Q9;
            Q9=makeQuery(id+"F1.opExtrude","CAP_EDGE",EDGE,{"disambiguationData":[OSD([sQuery(id+"F0.wireOp",EDGE,"E45")])],"isStart":true});
            var Q10;
            {var subQ0=sQuery(id+"F0.wireOp",EDGE,"E45");var subQ1=sQuery(id+"F0.wireOp",EDGE,"E23.MirrorCS");var subQ2=sQuery(id+"F0.wireOp",EDGE,"E1");Q10=makeQuery(id+"F1.opExtrude","CAP_EDGE",EDGE,{"disambiguationData":[OSD([subQ2]),TDD([makeQuery(id+"F0.imprint","IMPRINT",EDGE,{"disambiguationData":[TD([[makeQuery(id+"F0.imprint","INTERSECT",VERTEX,{"derivedFrom":[subQ2,subQ0]}),-1.0]])],"derivedFrom":subQ2}),makeQuery(id+"F0.imprint","IMPRINT",EDGE,{"disambiguationData":[TD([[makeQuery(id+"F0.imprint","INTERSECT",VERTEX,{"derivedFrom":[subQ2,subQ1]}),1.0]])],"derivedFrom":subQ2})])],"isStart":true});}
            var Q11;
            Q11=makeQuery(id+"F1.opExtrude","CAP_EDGE",EDGE,{"disambiguationData":[OSD([sQuery(id+"F0.wireOp",EDGE,"E23.MirrorCS")])],"isStart":true});
            var Q12;
            Q12=makeQuery(id+"F1.opExtrude","CAP_EDGE",EDGE,{"disambiguationData":[OSD([sQuery(id+"F0.wireOp",EDGE,"E26.MirrorCS")])],"isStart":true});
            var Q13;
            {var subQ0=sQuery(id+"F0.wireOp",EDGE,"E26.MirrorCS");var subQ1=sQuery(id+"F0.wireOp",EDGE,"E16.MirrorCS");var subQ2=sQuery(id+"F0.wireOp",EDGE,"E1");Q13=makeQuery(id+"F1.opExtrude","CAP_EDGE",EDGE,{"disambiguationData":[OSD([subQ2]),TDD([makeQuery(id+"F0.imprint","IMPRINT",EDGE,{"disambiguationData":[TD([[makeQuery(id+"F0.imprint","INTERSECT",VERTEX,{"derivedFrom":[subQ2,subQ1]}),1.0]])],"derivedFrom":subQ2}),makeQuery(id+"F0.imprint","IMPRINT",EDGE,{"disambiguationData":[TD([[makeQuery(id+"F0.imprint","INTERSECT",VERTEX,{"derivedFrom":[subQ2,subQ0]}),-1.0]])],"derivedFrom":subQ2})])],"isStart":true});}
            var Q14;
            Q14=makeQuery(id+"F1.opExtrude","CAP_EDGE",EDGE,{"disambiguationData":[OSD([sQuery(id+"F0.wireOp",EDGE,"E16.MirrorCS")])],"isStart":true});
            var Q15;
            Q15=makeQuery(id+"F1.opExtrude","CAP_EDGE",EDGE,{"disambiguationData":[OSD([sQuery(id+"F0.wireOp",EDGE,"E15")])],"isStart":true});
            var Q16;
            {var subQ0=sQuery(id+"F0.wireOp",EDGE,"E47.MirrorCS");var subQ1=sQuery(id+"F0.wireOp",EDGE,"E15");var subQ2=sQuery(id+"F0.wireOp",EDGE,"E1");Q16=makeQuery(id+"F1.opExtrude","CAP_EDGE",EDGE,{"disambiguationData":[OSD([subQ2]),TDD([makeQuery(id+"F0.imprint","IMPRINT",EDGE,{"disambiguationData":[TD([[makeQuery(id+"F0.imprint","INTERSECT",VERTEX,{"derivedFrom":[subQ2,subQ1]}),-1.0]])],"derivedFrom":subQ2}),makeQuery(id+"F0.imprint","IMPRINT",EDGE,{"disambiguationData":[TD([[makeQuery(id+"F0.imprint","INTERSECT",VERTEX,{"derivedFrom":[subQ2,subQ0]}),1.0]])],"derivedFrom":subQ2})])],"isStart":true});}
            var Q17;
            Q17=makeQuery(id+"F1.opExtrude","CAP_EDGE",EDGE,{"disambiguationData":[OSD([sQuery(id+"F0.wireOp",EDGE,"E47.MirrorCS")])],"isStart":true});
            fillet(context, id + "F7", {"entities" : qUnion([Q0, Q1, Q2, Q3, Q4, Q5, Q6, Q7, Q8, Q9, Q10, Q11, Q12, Q13, Q14, Q15, Q16, Q17]), "radius" : .5 * mm, "tangentPropagation" : true, "allowEdgeOverflow" : false});
        }
    });
